# Revit family: Gefälleblock 2,5 Grad BIG FOOT 330
name_source: partatom
category: HLS-Bauteile
units: mm (PartAtom-declared; Revit-internal decimal feet)

## family parameters
Arbeitsebenenbasiert = Ja
Beim Laden mit Abzugskörper schneiden = Nein
Bemaßung runder Anschluss = Durchmesser verwenden
Beschriftungsausrichtung beibehalten = Nein
Gemeinsam genutzt = Ja
Immer vertikal = Nein
Klassifizierung = Keine
Raumberechnungspunkt = Nein
Teiletyp = Normal

## types (1)
- Gefälleblock 2,5 Grad BIG FOOT 330
    Artikelnummer = 08197628
    Breite = 330 mm
    EAN = 4250928468932
    Fabrikat = MEFA
    Gewicht = 0,60 kg
    Gewicht pro Bauteil = 0,60 kg
    Höhe 1 = 12 mm
    Höhe 2 = 26 mm
    Kurztext1 = Gefälleblock BIG FOOT® 330
    Kurztext2 = Kunststoff 330x330x12 / 26 mm 2,5 °
    Länge = 330 mm
    Material = Kunststoff
    Materialname = Polyamid 6
    Mengeneinheit = St
    Neigung = 2.5 °
    Vorgabe-Ansicht = 1219 mm
    max. Temperaturbeständigkeit = 80 °C
    passend für = BIG FOOT® 330
    vpe = 1
